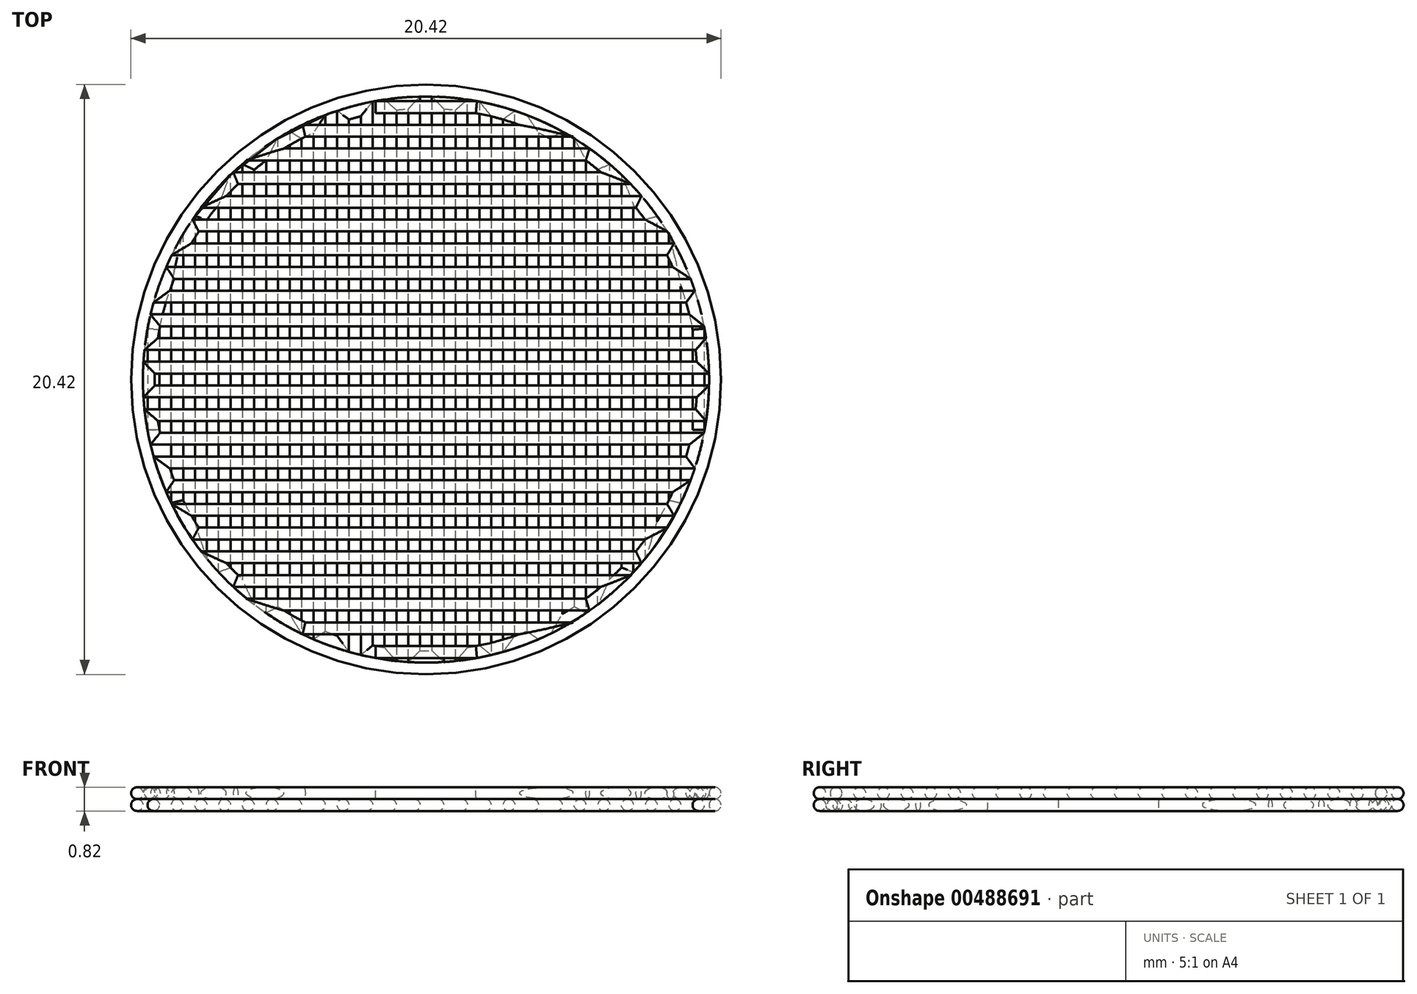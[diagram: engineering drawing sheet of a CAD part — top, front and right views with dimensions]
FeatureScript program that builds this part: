
annotation { "Feature Type Name" : "Feature", "Feature Type Description" : "" }
export const myFeature = defineFeature(function(context is Context, id is Id, definition is map)
    precondition{}
    {
        {
            assignVariable(context, id + "F0", {"name" : "d", "anyValue" : 0.4 * mm});
        }
        {
            var Q0;
            Q0=qCreatedBy(makeId("Top.planeOp"),FACE);
            cPlane(context, id + "F1", {"entities" : qUnion([Q0]), "cplaneType" : CPlaneType.OFFSET, "offset" : getVariable(context, 'd') / 2, "width" : 150 * mm, "height" : 150 * mm});
        }
        {
            var Q0;
            Q0=qCreatedBy(id+"F1.planeOp",FACE);
            var sketch = newSketch(context, id + "F2", { "sketchPlane" : qUnion([Q0])});
            skLineSegment(sketch, "E0.bottom", {"start": v(10, 10) * mm, "end": v(-10, 10) * mm});
            skLineSegment(sketch, "E0.top", {"start": v(10, -10) * mm, "end": v(-10, -10) * mm});
            skLineSegment(sketch, "E0.left", {"start": v(10, 10) * mm, "end": v(10, -10) * mm});
            skLineSegment(sketch, "E0.right", {"start": v(-10, 10) * mm, "end": v(-10, -10) * mm});
            skPoint(sketch, "E0.middle", {"position": v(0, 0) * mm});
            skLineSegment(sketch, "E1", {"start": v(10, -10) * mm, "end": v(9.43, -10) * mm});
            skLineSegment(sketch, "E2", {"start": v(9.43, -10) * mm, "end": v(8.6, -10) * mm});
            skLineSegment(sketch, "E3", {"start": v(8.6, -10) * mm, "end": v(7.8, -10) * mm});
            skLineSegment(sketch, "E4", {"start": v(7.8, -10) * mm, "end": v(6.97, -10) * mm});
            skLineSegment(sketch, "E5", {"start": v(6.97, -10) * mm, "end": v(6.15, -10) * mm});
            skLineSegment(sketch, "E6", {"start": v(6.15, -10) * mm, "end": v(5.33, -10) * mm});
            skLineSegment(sketch, "E7", {"start": v(5.33, -10) * mm, "end": v(4.5, -10) * mm});
            skLineSegment(sketch, "E8", {"start": v(4.5, -10) * mm, "end": v(3.69, -10) * mm});
            skLineSegment(sketch, "E9", {"start": v(3.69, -10) * mm, "end": v(2.87, -10) * mm});
            skLineSegment(sketch, "E10", {"start": v(2.87, -10) * mm, "end": v(2.05, -10) * mm});
            skLineSegment(sketch, "E11", {"start": v(2.05, -10) * mm, "end": v(1.23, -10) * mm});
            skLineSegment(sketch, "E12", {"start": v(-1.23, -10) * mm, "end": v(-2.05, -10) * mm});
            skLineSegment(sketch, "E13", {"start": v(-2.05, -10) * mm, "end": v(-2.87, -10) * mm});
            skLineSegment(sketch, "E14", {"start": v(-2.87, -10) * mm, "end": v(-3.69, -10) * mm});
            skLineSegment(sketch, "E15", {"start": v(-3.69, -10) * mm, "end": v(-4.5, -10) * mm});
            skLineSegment(sketch, "E16", {"start": v(-4.5, -10) * mm, "end": v(-5.33, -10) * mm});
            skLineSegment(sketch, "E17", {"start": v(-5.33, -10) * mm, "end": v(-6.15, -10) * mm});
            skLineSegment(sketch, "E18", {"start": v(-6.15, -10) * mm, "end": v(-6.97, -10) * mm});
            skLineSegment(sketch, "E19", {"start": v(-6.97, -10) * mm, "end": v(-7.8, -10) * mm});
            skLineSegment(sketch, "E20", {"start": v(-7.8, -10) * mm, "end": v(-8.6, -10) * mm});
            skLineSegment(sketch, "E21", {"start": v(-8.6, -10) * mm, "end": v(-9.43, -10) * mm});
            skLineSegment(sketch, "E22", {"start": v(-9.43, -10) * mm, "end": v(-10, -10) * mm});
            skLineSegment(sketch, "E23", {"start": v(9.43, -10) * mm, "end": v(9.43, -1.74) * mm});
            skLineSegment(sketch, "E24", {"start": v(9.43, -1.74) * mm, "end": v(9.43, 1.74) * mm});
            skLineSegment(sketch, "E25", {"start": v(9.43, 1.74) * mm, "end": v(9.43, 10) * mm});
            skLineSegment(sketch, "E26", {"start": v(9.43, 10) * mm, "end": v(10, 10) * mm});
            skLineSegment(sketch, "E27", {"start": v(8.6, -10) * mm, "end": v(8.6, -4.22) * mm});
            skLineSegment(sketch, "E28", {"start": v(8.6, -4.22) * mm, "end": v(8.6, 4.22) * mm});
            skLineSegment(sketch, "E29", {"start": v(8.6, 4.22) * mm, "end": v(8.6, 10) * mm});
            skLineSegment(sketch, "E30", {"start": v(8.6, 10) * mm, "end": v(9.43, 10) * mm});
            skLineSegment(sketch, "E31", {"start": v(7.8, -10) * mm, "end": v(7.8, -5.6) * mm});
            skLineSegment(sketch, "E32", {"start": v(7.8, -5.6) * mm, "end": v(7.8, 5.6) * mm});
            skLineSegment(sketch, "E33", {"start": v(7.8, 5.6) * mm, "end": v(7.8, 10) * mm});
            skLineSegment(sketch, "E34", {"start": v(7.79, 10) * mm, "end": v(8.6, 10) * mm});
            skLineSegment(sketch, "E35", {"start": v(6.97, -10) * mm, "end": v(6.97, -6.59) * mm});
            skLineSegment(sketch, "E36", {"start": v(6.97, -6.59) * mm, "end": v(6.97, 6.59) * mm});
            skLineSegment(sketch, "E37", {"start": v(6.97, 6.59) * mm, "end": v(6.97, 10) * mm});
            skLineSegment(sketch, "E38", {"start": v(6.97, 10) * mm, "end": v(7.79, 10) * mm});
            skLineSegment(sketch, "E39", {"start": v(6.15, -10) * mm, "end": v(6.15, -7.36) * mm});
            skLineSegment(sketch, "E40", {"start": v(6.15, -7.36) * mm, "end": v(6.15, 7.36) * mm});
            skLineSegment(sketch, "E41", {"start": v(6.15, 7.36) * mm, "end": v(6.15, 10) * mm});
            skLineSegment(sketch, "E42", {"start": v(6.15, 10) * mm, "end": v(6.97, 10) * mm});
            skLineSegment(sketch, "E43", {"start": v(5.33, -10) * mm, "end": v(5.33, -7.97) * mm});
            skLineSegment(sketch, "E44", {"start": v(5.33, -7.97) * mm, "end": v(5.33, 7.97) * mm});
            skLineSegment(sketch, "E45", {"start": v(5.33, 7.97) * mm, "end": v(5.33, 10) * mm});
            skLineSegment(sketch, "E46", {"start": v(5.33, 10) * mm, "end": v(6.15, 10) * mm});
            skLineSegment(sketch, "E47", {"start": v(4.5, -10) * mm, "end": v(4.5, -8.46) * mm});
            skLineSegment(sketch, "E48", {"start": v(4.5, -8.46) * mm, "end": v(4.5, 8.46) * mm});
            skLineSegment(sketch, "E49", {"start": v(4.5, 8.46) * mm, "end": v(4.5, 10) * mm});
            skLineSegment(sketch, "E50", {"start": v(4.5, 10) * mm, "end": v(5.33, 10) * mm});
            skLineSegment(sketch, "E51", {"start": v(3.69, -10) * mm, "end": v(3.69, -8.85) * mm});
            skLineSegment(sketch, "E52", {"start": v(3.69, -8.85) * mm, "end": v(3.69, 8.85) * mm});
            skLineSegment(sketch, "E53", {"start": v(3.69, 8.85) * mm, "end": v(3.69, 10) * mm});
            skLineSegment(sketch, "E54", {"start": v(3.69, 10) * mm, "end": v(4.5, 10) * mm});
            skLineSegment(sketch, "E55", {"start": v(2.87, -10) * mm, "end": v(2.87, -9.15) * mm});
            skLineSegment(sketch, "E56", {"start": v(2.87, -9.15) * mm, "end": v(2.87, 9.15) * mm});
            skLineSegment(sketch, "E57", {"start": v(2.87, 9.15) * mm, "end": v(2.87, 10) * mm});
            skLineSegment(sketch, "E58", {"start": v(2.87, 10) * mm, "end": v(3.69, 10) * mm});
            skLineSegment(sketch, "E59", {"start": v(2.05, -10) * mm, "end": v(2.05, -9.37) * mm});
            skLineSegment(sketch, "E60", {"start": v(2.05, -9.37) * mm, "end": v(2.05, 9.37) * mm});
            skLineSegment(sketch, "E61", {"start": v(2.05, 9.37) * mm, "end": v(2.05, 10) * mm});
            skLineSegment(sketch, "E62", {"start": v(2.05, 10) * mm, "end": v(2.87, 10) * mm});
            skLineSegment(sketch, "E63", {"start": v(1.23, -10) * mm, "end": v(1.23, -9.51) * mm});
            skLineSegment(sketch, "E64", {"start": v(1.23, -9.51) * mm, "end": v(1.23, 9.51) * mm});
            skLineSegment(sketch, "E65", {"start": v(1.23, 9.51) * mm, "end": v(1.23, 10) * mm});
            skLineSegment(sketch, "E66", {"start": v(1.23, 10) * mm, "end": v(2.05, 10) * mm});
            skLineSegment(sketch, "E67", {"start": v(-1.23, -10) * mm, "end": v(-1.23, -9.51) * mm});
            skLineSegment(sketch, "E68", {"start": v(-1.23, -9.51) * mm, "end": v(-1.23, 9.51) * mm});
            skLineSegment(sketch, "E69", {"start": v(-1.23, 9.51) * mm, "end": v(-1.23, 10) * mm});
            skLineSegment(sketch, "E70", {"start": v(-2.05, -10) * mm, "end": v(-2.05, -9.37) * mm});
            skLineSegment(sketch, "E71", {"start": v(-2.05, -9.37) * mm, "end": v(-2.05, 9.37) * mm});
            skLineSegment(sketch, "E72", {"start": v(-2.05, 9.37) * mm, "end": v(-2.05, 10) * mm});
            skLineSegment(sketch, "E73", {"start": v(-2.05, 10) * mm, "end": v(-1.23, 10) * mm});
            skLineSegment(sketch, "E74", {"start": v(-2.87, -10) * mm, "end": v(-2.87, -9.15) * mm});
            skLineSegment(sketch, "E75", {"start": v(-2.87, -9.15) * mm, "end": v(-2.87, 9.15) * mm});
            skLineSegment(sketch, "E76", {"start": v(-2.87, 9.15) * mm, "end": v(-2.87, 10) * mm});
            skLineSegment(sketch, "E77", {"start": v(-2.87, 10) * mm, "end": v(-2.05, 10) * mm});
            skLineSegment(sketch, "E78", {"start": v(-3.69, -10) * mm, "end": v(-3.69, -8.85) * mm});
            skLineSegment(sketch, "E79", {"start": v(-3.69, -8.85) * mm, "end": v(-3.69, 8.85) * mm});
            skLineSegment(sketch, "E80", {"start": v(-3.69, 8.85) * mm, "end": v(-3.69, 10) * mm});
            skLineSegment(sketch, "E81", {"start": v(-3.69, 10) * mm, "end": v(-2.87, 10) * mm});
            skLineSegment(sketch, "E82", {"start": v(-4.5, -10) * mm, "end": v(-4.5, -8.46) * mm});
            skLineSegment(sketch, "E83", {"start": v(-4.5, -8.46) * mm, "end": v(-4.5, 8.46) * mm});
            skLineSegment(sketch, "E84", {"start": v(-4.5, 8.46) * mm, "end": v(-4.5, 10) * mm});
            skLineSegment(sketch, "E85", {"start": v(-4.5, 10) * mm, "end": v(-3.69, 10) * mm});
            skLineSegment(sketch, "E86", {"start": v(-5.33, -10) * mm, "end": v(-5.33, -7.97) * mm});
            skLineSegment(sketch, "E87", {"start": v(-5.33, -7.97) * mm, "end": v(-5.33, 7.97) * mm});
            skLineSegment(sketch, "E88", {"start": v(-5.33, 7.97) * mm, "end": v(-5.33, 10) * mm});
            skLineSegment(sketch, "E89", {"start": v(-5.33, 10) * mm, "end": v(-4.5, 10) * mm});
            skLineSegment(sketch, "E90", {"start": v(-6.15, -10) * mm, "end": v(-6.15, -7.36) * mm});
            skLineSegment(sketch, "E91", {"start": v(-6.15, -7.36) * mm, "end": v(-6.15, 7.36) * mm});
            skLineSegment(sketch, "E92", {"start": v(-6.15, 7.36) * mm, "end": v(-6.15, 10) * mm});
            skLineSegment(sketch, "E93", {"start": v(-6.15, 10) * mm, "end": v(-5.33, 10) * mm});
            skLineSegment(sketch, "E94", {"start": v(-6.97, -10) * mm, "end": v(-6.97, -6.59) * mm});
            skLineSegment(sketch, "E95", {"start": v(-6.97, -6.59) * mm, "end": v(-6.97, 6.59) * mm});
            skLineSegment(sketch, "E96", {"start": v(-6.97, 6.59) * mm, "end": v(-6.97, 10) * mm});
            skLineSegment(sketch, "E97", {"start": v(-6.97, 10) * mm, "end": v(-6.15, 10) * mm});
            skLineSegment(sketch, "E98", {"start": v(-7.8, -10) * mm, "end": v(-7.8, -5.6) * mm});
            skLineSegment(sketch, "E99", {"start": v(-7.8, -5.6) * mm, "end": v(-7.8, 5.6) * mm});
            skLineSegment(sketch, "E100", {"start": v(-7.8, 5.6) * mm, "end": v(-7.8, 10) * mm});
            skLineSegment(sketch, "E101", {"start": v(-7.8, 10) * mm, "end": v(-6.97, 10) * mm});
            skLineSegment(sketch, "E102", {"start": v(-8.6, -10) * mm, "end": v(-8.6, -4.22) * mm});
            skLineSegment(sketch, "E103", {"start": v(-8.6, -4.22) * mm, "end": v(-8.6, 4.22) * mm});
            skLineSegment(sketch, "E104", {"start": v(-8.6, 4.22) * mm, "end": v(-8.6, 10) * mm});
            skLineSegment(sketch, "E105", {"start": v(-8.6, 10) * mm, "end": v(-7.8, 10) * mm});
            skLineSegment(sketch, "E106", {"start": v(-9.43, -10) * mm, "end": v(-9.43, -1.74) * mm});
            skLineSegment(sketch, "E107", {"start": v(-9.43, -1.74) * mm, "end": v(-9.43, 1.74) * mm});
            skLineSegment(sketch, "E108", {"start": v(-9.43, 1.74) * mm, "end": v(-9.43, 10) * mm});
            skLineSegment(sketch, "E109", {"start": v(-9.43, 10) * mm, "end": v(-8.6, 10) * mm});
            skLineSegment(sketch, "E110", {"start": v(-10, 10) * mm, "end": v(-9.43, 10) * mm});
            skArc(sketch, "E111", {"start": v(9.43, 1.74) * mm, "mid": v(9.1, 3.01) * mm, "end": v(8.61, 4.22) * mm});
            skArc(sketch, "E112", {"start": v(7.8, 5.6) * mm, "mid": v(7.4, 6.1) * mm, "end": v(6.97, 6.59) * mm});
            skArc(sketch, "E113", {"start": v(6.15, 7.36) * mm, "mid": v(5.75, 7.68) * mm, "end": v(5.33, 7.97) * mm});
            skArc(sketch, "E114", {"start": v(4.51, 8.46) * mm, "mid": v(4.1, 8.67) * mm, "end": v(3.7, 8.85) * mm});
            skArc(sketch, "E115", {"start": v(2.87, 9.15) * mm, "mid": v(2.46, 9.27) * mm, "end": v(2.05, 9.37) * mm});
            skArc(sketch, "E116", {"start": v(1.23, -9.51) * mm, "mid": v(1.64, -9.45) * mm, "end": v(2.05, -9.37) * mm});
            skArc(sketch, "E117", {"start": v(2.87, -9.15) * mm, "mid": v(3.28, -9.01) * mm, "end": v(3.69, -8.85) * mm});
            skArc(sketch, "E118", {"start": v(4.51, -8.46) * mm, "mid": v(4.93, -8.23) * mm, "end": v(5.33, -7.97) * mm});
            skArc(sketch, "E119", {"start": v(6.15, -7.36) * mm, "mid": v(6.57, -6.98) * mm, "end": v(6.97, -6.59) * mm});
            skArc(sketch, "E120", {"start": v(7.8, -5.6) * mm, "mid": v(8.23, -4.93) * mm, "end": v(8.6, -4.22) * mm});
            skLineSegment(sketch, "E121", {"start": v(1.23, -10) * mm, "end": v(0.4, -10) * mm});
            skLineSegment(sketch, "E122", {"start": v(0.4, -10) * mm, "end": v(-0.4, -10) * mm});
            skLineSegment(sketch, "E123", {"start": v(-0.4, -10) * mm, "end": v(-1.23, -10) * mm});
            skLineSegment(sketch, "E124", {"start": v(0.4, -10) * mm, "end": v(0.4, -9.58) * mm});
            skLineSegment(sketch, "E125", {"start": v(0.4, -9.58) * mm, "end": v(0.4, 9.58) * mm});
            skLineSegment(sketch, "E126", {"start": v(0.4, 9.58) * mm, "end": v(0.4, 10) * mm});
            skLineSegment(sketch, "E127", {"start": v(0.4, 10) * mm, "end": v(1.23, 10) * mm});
            skLineSegment(sketch, "E128", {"start": v(0.4, 10) * mm, "end": v(-0.4, 10) * mm});
            skLineSegment(sketch, "E129", {"start": v(-0.4, 10) * mm, "end": v(-1.23, 10) * mm});
            skLineSegment(sketch, "E130", {"start": v(-0.4, 10) * mm, "end": v(-0.4, 9.58) * mm});
            skLineSegment(sketch, "E131", {"start": v(-0.4, 9.58) * mm, "end": v(-0.4, -9.58) * mm});
            skLineSegment(sketch, "E132", {"start": v(-0.41, -9.58) * mm, "end": v(-0.4, -10) * mm});
            skCircle(sketch, "E133", {"center": v(0, 0) * mm, "radius": 10 * mm});
            skArc(sketch, "E134", {"start": v(1.23, 9.51) * mm, "mid": v(0.82, 9.55) * mm, "end": v(0.41, 9.58) * mm});
            skArc(sketch, "E135", {"start": v(-0.4, 9.58) * mm, "mid": v(-0.82, 9.55) * mm, "end": v(-1.23, 9.51) * mm});
            skArc(sketch, "E136", {"start": v(-2.05, 9.37) * mm, "mid": v(-2.46, 9.27) * mm, "end": v(-2.87, 9.15) * mm});
            skArc(sketch, "E137", {"start": v(-3.69, 8.85) * mm, "mid": v(-4.1, 8.67) * mm, "end": v(-4.51, 8.46) * mm});
            skArc(sketch, "E138", {"start": v(-5.33, 7.97) * mm, "mid": v(-5.75, 7.68) * mm, "end": v(-6.15, 7.36) * mm});
            skArc(sketch, "E139", {"start": v(-6.97, 6.59) * mm, "mid": v(-7.4, 6.1) * mm, "end": v(-7.79, 5.6) * mm});
            skArc(sketch, "E140", {"start": v(-8.6, 4.22) * mm, "mid": v(-9.1, 3.01) * mm, "end": v(-9.43, 1.74) * mm});
            skArc(sketch, "E141", {"start": v(0.41, -9.58) * mm, "mid": v(0, -9.6) * mm, "end": v(-0.4, -9.58) * mm});
            skArc(sketch, "E142", {"start": v(-1.23, -9.51) * mm, "mid": v(-1.64, -9.45) * mm, "end": v(-2.05, -9.37) * mm});
            skArc(sketch, "E143", {"start": v(-2.87, -9.15) * mm, "mid": v(-3.28, -9.01) * mm, "end": v(-3.69, -8.85) * mm});
            skArc(sketch, "E144", {"start": v(-4.51, -8.46) * mm, "mid": v(-4.93, -8.23) * mm, "end": v(-5.33, -7.97) * mm});
            skArc(sketch, "E145", {"start": v(-6.15, -7.36) * mm, "mid": v(-6.57, -6.98) * mm, "end": v(-6.97, -6.59) * mm});
            skArc(sketch, "E146", {"start": v(-7.8, -5.6) * mm, "mid": v(-8.23, -4.93) * mm, "end": v(-8.61, -4.22) * mm});
            skSolve(sketch);
        }
        {
            var Q0;
            Q0=qCreatedBy(makeId("Front.planeOp"),FACE);
            var sketch = newSketch(context, id + "F3", { "sketchPlane" : qUnion([Q0])});
            skCircle(sketch, "E147", {"center": v(-10, 0.2) * mm, "radius": 0.2 * mm});
            skSolve(sketch);
        }
        {
            var Q0;
            Q0=makeQuery(id+"F3.imprint","IMPRINT",FACE,{"disambiguationData":[TD([[makeQuery(id+"F3.imprint","IMPRINT",EDGE,{"derivedFrom":sQuery(id+"F3.wireOp",EDGE,"E147")}),1.0]])]});
            var Q1;
            Q1=sQuery(id+"F3.wireOp",EDGE,"E147");
            var Q2;
            Q2=sQuery(id+"F2.wireOp",EDGE,"E133");
            sweep(context, id + "F4", {"profiles" : qUnion([Q0]), "surfaceProfiles" : qUnion([Q1]), "path" : qUnion([Q2])});
        }
        {
            var Q0;
            Q0=sQuery(id+"F2.wireOp",EDGE,"E24");
            var Q1;
            Q1=sQuery(id+"F2.wireOp",VERTEX,"E24.start");
            cPlane(context, id + "F5", {"entities" : qUnion([Q0, Q1]), "cplaneType" : CPlaneType.LINE_POINT, "offset" : 25 * mm, "width" : 150 * mm, "height" : 150 * mm});
        }
        {
            var Q0;
            Q0=qCreatedBy(id+"F5.planeOp",FACE);
            var sketch = newSketch(context, id + "F6", { "sketchPlane" : qUnion([Q0])});
            skCircle(sketch, "E148", {"center": v(-9.43, 0.2) * mm, "radius": 0.2 * mm});
            skSolve(sketch);
        }
        {
            var Q0;
            Q0=qSketchRegion(id+"F6",true);
            var Q1;
            Q1=sQuery(id+"F2.wireOp",EDGE,"E24");
            var Q2;
            Q2=sQuery(id+"F2.wireOp",EDGE,"E111");
            var Q3;
            Q3=sQuery(id+"F2.wireOp",EDGE,"E112");
            var Q4;
            Q4=sQuery(id+"F2.wireOp",EDGE,"E113");
            var Q5;
            Q5=sQuery(id+"F2.wireOp",EDGE,"E114");
            var Q6;
            Q6=sQuery(id+"F2.wireOp",EDGE,"E115");
            var Q7;
            Q7=sQuery(id+"F2.wireOp",EDGE,"E134");
            var Q8;
            Q8=sQuery(id+"F2.wireOp",EDGE,"E135");
            var Q9;
            Q9=sQuery(id+"F2.wireOp",EDGE,"E136");
            var Q10;
            Q10=sQuery(id+"F2.wireOp",EDGE,"E137");
            var Q11;
            Q11=sQuery(id+"F2.wireOp",EDGE,"E138");
            var Q12;
            Q12=sQuery(id+"F2.wireOp",EDGE,"E139");
            var Q13;
            Q13=sQuery(id+"F2.wireOp",EDGE,"E140");
            var Q14;
            Q14=sQuery(id+"F2.wireOp",EDGE,"E107");
            var Q15;
            Q15=sQuery(id+"F2.wireOp",EDGE,"E146");
            var Q16;
            Q16=sQuery(id+"F2.wireOp",EDGE,"E145");
            var Q17;
            Q17=sQuery(id+"F2.wireOp",EDGE,"E144");
            var Q18;
            Q18=sQuery(id+"F2.wireOp",EDGE,"E143");
            var Q19;
            Q19=sQuery(id+"F2.wireOp",EDGE,"E142");
            var Q20;
            Q20=sQuery(id+"F2.wireOp",EDGE,"E141");
            var Q21;
            Q21=sQuery(id+"F2.wireOp",EDGE,"E116");
            var Q22;
            Q22=sQuery(id+"F2.wireOp",EDGE,"E117");
            var Q23;
            Q23=sQuery(id+"F2.wireOp",EDGE,"E118");
            var Q24;
            Q24=sQuery(id+"F2.wireOp",EDGE,"E119");
            var Q25;
            Q25=sQuery(id+"F2.wireOp",EDGE,"E120");
            var Q26;
            Q26=sQuery(id+"F2.wireOp",EDGE,"E28");
            var Q27;
            Q27=sQuery(id+"F2.wireOp",EDGE,"E32");
            var Q28;
            Q28=sQuery(id+"F2.wireOp",EDGE,"E36");
            var Q29;
            Q29=sQuery(id+"F2.wireOp",EDGE,"E40");
            var Q30;
            Q30=sQuery(id+"F2.wireOp",EDGE,"E44");
            var Q31;
            Q31=sQuery(id+"F2.wireOp",EDGE,"E48");
            var Q32;
            Q32=sQuery(id+"F2.wireOp",EDGE,"E52");
            var Q33;
            Q33=sQuery(id+"F2.wireOp",EDGE,"E56");
            var Q34;
            Q34=sQuery(id+"F2.wireOp",EDGE,"E60");
            var Q35;
            Q35=sQuery(id+"F2.wireOp",EDGE,"E64");
            var Q36;
            Q36=sQuery(id+"F2.wireOp",EDGE,"E125");
            var Q37;
            Q37=sQuery(id+"F2.wireOp",EDGE,"E131");
            var Q38;
            Q38=sQuery(id+"F2.wireOp",EDGE,"E68");
            var Q39;
            Q39=sQuery(id+"F2.wireOp",EDGE,"E71");
            var Q40;
            Q40=sQuery(id+"F2.wireOp",EDGE,"E75");
            var Q41;
            Q41=sQuery(id+"F2.wireOp",EDGE,"E79");
            var Q42;
            Q42=sQuery(id+"F2.wireOp",EDGE,"E83");
            var Q43;
            Q43=sQuery(id+"F2.wireOp",EDGE,"E87");
            var Q44;
            Q44=sQuery(id+"F2.wireOp",EDGE,"E91");
            var Q45;
            Q45=sQuery(id+"F2.wireOp",EDGE,"E95");
            var Q46;
            Q46=sQuery(id+"F2.wireOp",EDGE,"E99");
            var Q47;
            Q47=sQuery(id+"F2.wireOp",EDGE,"E103");
            sweep(context, id + "F7", {"profiles" : qUnion([Q0]), "path" : qUnion([Q1, Q2, Q3, Q4, Q5, Q6, Q7, Q8, Q9, Q10, Q11, Q12, Q13, Q14, Q15, Q16, Q17, Q18, Q19, Q20, Q21, Q22, Q23, Q24, Q25, Q26, Q27, Q28, Q29, Q30, Q31, Q32, Q33, Q34, Q35, Q36, Q37, Q38, Q39, Q40, Q41, Q42, Q43, Q44, Q45, Q46, Q47])});
        }
        {
            var Q0;
            Q0=qCreatedBy(id+"F1.planeOp",FACE);
            cPlane(context, id + "F8", {"entities" : qUnion([Q0]), "cplaneType" : CPlaneType.OFFSET, "offset" : getVariable(context, 'd'), "width" : 150 * mm, "height" : 150 * mm});
        }
        {
            var Q0;
            Q0=qCreatedBy(id+"F8.planeOp",FACE);
            var sketch = newSketch(context, id + "F9", { "sketchPlane" : qUnion([Q0])});
            skLineSegment(sketch, "E149.bottom", {"start": v(10, -10) * mm, "end": v(10, 10) * mm});
            skLineSegment(sketch, "E149.top", {"start": v(-10, -10) * mm, "end": v(-10, 10) * mm});
            skLineSegment(sketch, "E149.left", {"start": v(10, -10) * mm, "end": v(-10, -10) * mm});
            skLineSegment(sketch, "E149.right", {"start": v(10, 10) * mm, "end": v(-10, 10) * mm});
            skPoint(sketch, "E149.middle", {"position": v(0, 0) * mm});
            skLineSegment(sketch, "E150", {"start": v(-10, -10) * mm, "end": v(-10, -9.43) * mm});
            skLineSegment(sketch, "E151", {"start": v(-10, -9.43) * mm, "end": v(-10, -8.6) * mm});
            skLineSegment(sketch, "E152", {"start": v(-10, -8.6) * mm, "end": v(-10, -7.8) * mm});
            skLineSegment(sketch, "E153", {"start": v(-10, -7.8) * mm, "end": v(-10, -6.97) * mm});
            skLineSegment(sketch, "E154", {"start": v(-10, -6.97) * mm, "end": v(-10, -6.15) * mm});
            skLineSegment(sketch, "E155", {"start": v(-10, -6.15) * mm, "end": v(-10, -5.33) * mm});
            skLineSegment(sketch, "E156", {"start": v(-10, -5.33) * mm, "end": v(-10, -4.51) * mm});
            skLineSegment(sketch, "E157", {"start": v(-10, -4.51) * mm, "end": v(-10, -3.7) * mm});
            skLineSegment(sketch, "E158", {"start": v(-10, -3.7) * mm, "end": v(-10, -2.87) * mm});
            skLineSegment(sketch, "E159", {"start": v(-10, -2.87) * mm, "end": v(-10, -2.05) * mm});
            skLineSegment(sketch, "E160", {"start": v(-10, -2.05) * mm, "end": v(-10, -1.23) * mm});
            skLineSegment(sketch, "E161", {"start": v(-10, 1.23) * mm, "end": v(-10, 2.05) * mm});
            skLineSegment(sketch, "E162", {"start": v(-10, 2.05) * mm, "end": v(-10, 2.87) * mm});
            skLineSegment(sketch, "E163", {"start": v(-10, 2.87) * mm, "end": v(-10, 3.7) * mm});
            skLineSegment(sketch, "E164", {"start": v(-10, 3.7) * mm, "end": v(-10, 4.51) * mm});
            skLineSegment(sketch, "E165", {"start": v(-10, 4.51) * mm, "end": v(-10, 5.33) * mm});
            skLineSegment(sketch, "E166", {"start": v(-10, 5.33) * mm, "end": v(-10, 6.15) * mm});
            skLineSegment(sketch, "E167", {"start": v(-10, 6.15) * mm, "end": v(-10, 6.97) * mm});
            skLineSegment(sketch, "E168", {"start": v(-10, 6.97) * mm, "end": v(-10, 7.8) * mm});
            skLineSegment(sketch, "E169", {"start": v(-10, 7.8) * mm, "end": v(-10, 8.61) * mm});
            skLineSegment(sketch, "E170", {"start": v(-10, 8.61) * mm, "end": v(-10, 9.43) * mm});
            skLineSegment(sketch, "E171", {"start": v(-10, 9.43) * mm, "end": v(-10, 10) * mm});
            skLineSegment(sketch, "E172", {"start": v(-10, -9.43) * mm, "end": v(-1.74, -9.43) * mm});
            skLineSegment(sketch, "E173", {"start": v(-1.74, -9.43) * mm, "end": v(1.74, -9.43) * mm});
            skLineSegment(sketch, "E174", {"start": v(1.74, -9.43) * mm, "end": v(10, -9.43) * mm});
            skLineSegment(sketch, "E175", {"start": v(10, -9.43) * mm, "end": v(10, -10) * mm});
            skLineSegment(sketch, "E176", {"start": v(-10, -8.6) * mm, "end": v(-4.22, -8.6) * mm});
            skLineSegment(sketch, "E177", {"start": v(-4.22, -8.6) * mm, "end": v(4.22, -8.6) * mm});
            skLineSegment(sketch, "E178", {"start": v(4.22, -8.6) * mm, "end": v(10, -8.6) * mm});
            skLineSegment(sketch, "E179", {"start": v(10, -8.6) * mm, "end": v(10, -9.43) * mm});
            skLineSegment(sketch, "E180", {"start": v(-10, -7.8) * mm, "end": v(-5.6, -7.8) * mm});
            skLineSegment(sketch, "E181", {"start": v(-5.6, -7.8) * mm, "end": v(5.6, -7.8) * mm});
            skLineSegment(sketch, "E182", {"start": v(5.6, -7.8) * mm, "end": v(10, -7.8) * mm});
            skLineSegment(sketch, "E183", {"start": v(10, -7.8) * mm, "end": v(10, -8.6) * mm});
            skLineSegment(sketch, "E184", {"start": v(-10, -6.97) * mm, "end": v(-6.59, -6.97) * mm});
            skLineSegment(sketch, "E185", {"start": v(-6.59, -6.97) * mm, "end": v(6.59, -6.97) * mm});
            skLineSegment(sketch, "E186", {"start": v(6.59, -6.97) * mm, "end": v(10, -6.97) * mm});
            skLineSegment(sketch, "E187", {"start": v(10, -6.97) * mm, "end": v(10, -7.8) * mm});
            skLineSegment(sketch, "E188", {"start": v(-10, -6.15) * mm, "end": v(-7.36, -6.15) * mm});
            skLineSegment(sketch, "E189", {"start": v(-7.36, -6.15) * mm, "end": v(7.36, -6.15) * mm});
            skLineSegment(sketch, "E190", {"start": v(7.36, -6.15) * mm, "end": v(10, -6.15) * mm});
            skLineSegment(sketch, "E191", {"start": v(10, -6.15) * mm, "end": v(10, -6.97) * mm});
            skLineSegment(sketch, "E192", {"start": v(-10, -5.33) * mm, "end": v(-7.97, -5.33) * mm});
            skLineSegment(sketch, "E193", {"start": v(-7.97, -5.33) * mm, "end": v(7.97, -5.33) * mm});
            skLineSegment(sketch, "E194", {"start": v(7.97, -5.33) * mm, "end": v(10, -5.33) * mm});
            skLineSegment(sketch, "E195", {"start": v(10, -5.33) * mm, "end": v(10, -6.15) * mm});
            skLineSegment(sketch, "E196", {"start": v(-10, -4.51) * mm, "end": v(-8.46, -4.51) * mm});
            skLineSegment(sketch, "E197", {"start": v(-8.46, -4.51) * mm, "end": v(8.46, -4.51) * mm});
            skLineSegment(sketch, "E198", {"start": v(8.46, -4.51) * mm, "end": v(10, -4.51) * mm});
            skLineSegment(sketch, "E199", {"start": v(10, -4.51) * mm, "end": v(10, -5.33) * mm});
            skLineSegment(sketch, "E200", {"start": v(-10, -3.7) * mm, "end": v(-8.85, -3.7) * mm});
            skLineSegment(sketch, "E201", {"start": v(-8.85, -3.7) * mm, "end": v(8.85, -3.7) * mm});
            skLineSegment(sketch, "E202", {"start": v(8.85, -3.7) * mm, "end": v(10, -3.7) * mm});
            skLineSegment(sketch, "E203", {"start": v(10, -3.7) * mm, "end": v(10, -4.51) * mm});
            skLineSegment(sketch, "E204", {"start": v(-10, -2.87) * mm, "end": v(-9.15, -2.87) * mm});
            skLineSegment(sketch, "E205", {"start": v(-9.15, -2.87) * mm, "end": v(9.15, -2.87) * mm});
            skLineSegment(sketch, "E206", {"start": v(9.15, -2.87) * mm, "end": v(10, -2.87) * mm});
            skLineSegment(sketch, "E207", {"start": v(10, -2.87) * mm, "end": v(10, -3.7) * mm});
            skLineSegment(sketch, "E208", {"start": v(-10, -2.05) * mm, "end": v(-9.37, -2.05) * mm});
            skLineSegment(sketch, "E209", {"start": v(-9.37, -2.05) * mm, "end": v(9.37, -2.05) * mm});
            skLineSegment(sketch, "E210", {"start": v(9.37, -2.05) * mm, "end": v(10, -2.05) * mm});
            skLineSegment(sketch, "E211", {"start": v(10, -2.05) * mm, "end": v(10, -2.87) * mm});
            skLineSegment(sketch, "E212", {"start": v(-10, -1.23) * mm, "end": v(-9.51, -1.23) * mm});
            skLineSegment(sketch, "E213", {"start": v(-9.51, -1.23) * mm, "end": v(9.51, -1.23) * mm});
            skLineSegment(sketch, "E214", {"start": v(9.51, -1.23) * mm, "end": v(10, -1.23) * mm});
            skLineSegment(sketch, "E215", {"start": v(10, -1.23) * mm, "end": v(10, -2.05) * mm});
            skLineSegment(sketch, "E216", {"start": v(-10, 1.23) * mm, "end": v(-9.51, 1.23) * mm});
            skLineSegment(sketch, "E217", {"start": v(-9.51, 1.23) * mm, "end": v(9.51, 1.23) * mm});
            skLineSegment(sketch, "E218", {"start": v(9.51, 1.23) * mm, "end": v(10, 1.23) * mm});
            skLineSegment(sketch, "E219", {"start": v(-10, 2.05) * mm, "end": v(-9.37, 2.05) * mm});
            skLineSegment(sketch, "E220", {"start": v(-9.37, 2.05) * mm, "end": v(9.37, 2.05) * mm});
            skLineSegment(sketch, "E221", {"start": v(9.37, 2.05) * mm, "end": v(10, 2.05) * mm});
            skLineSegment(sketch, "E222", {"start": v(10, 2.05) * mm, "end": v(10, 1.23) * mm});
            skLineSegment(sketch, "E223", {"start": v(-10, 2.87) * mm, "end": v(-9.15, 2.87) * mm});
            skLineSegment(sketch, "E224", {"start": v(-9.15, 2.87) * mm, "end": v(9.15, 2.87) * mm});
            skLineSegment(sketch, "E225", {"start": v(9.15, 2.87) * mm, "end": v(10, 2.87) * mm});
            skLineSegment(sketch, "E226", {"start": v(10, 2.87) * mm, "end": v(10, 2.05) * mm});
            skLineSegment(sketch, "E227", {"start": v(-10, 3.7) * mm, "end": v(-8.85, 3.7) * mm});
            skLineSegment(sketch, "E228", {"start": v(-8.85, 3.7) * mm, "end": v(8.85, 3.7) * mm});
            skLineSegment(sketch, "E229", {"start": v(8.85, 3.7) * mm, "end": v(10, 3.7) * mm});
            skLineSegment(sketch, "E230", {"start": v(10, 3.7) * mm, "end": v(10, 2.87) * mm});
            skLineSegment(sketch, "E231", {"start": v(-10, 4.51) * mm, "end": v(-8.46, 4.51) * mm});
            skLineSegment(sketch, "E232", {"start": v(-8.46, 4.51) * mm, "end": v(8.46, 4.51) * mm});
            skLineSegment(sketch, "E233", {"start": v(8.46, 4.51) * mm, "end": v(10, 4.51) * mm});
            skLineSegment(sketch, "E234", {"start": v(10, 4.51) * mm, "end": v(10, 3.7) * mm});
            skLineSegment(sketch, "E235", {"start": v(-10, 5.33) * mm, "end": v(-7.97, 5.33) * mm});
            skLineSegment(sketch, "E236", {"start": v(-7.97, 5.33) * mm, "end": v(7.97, 5.33) * mm});
            skLineSegment(sketch, "E237", {"start": v(7.97, 5.33) * mm, "end": v(10, 5.33) * mm});
            skLineSegment(sketch, "E238", {"start": v(10, 5.33) * mm, "end": v(10, 4.51) * mm});
            skLineSegment(sketch, "E239", {"start": v(-10, 6.15) * mm, "end": v(-7.36, 6.15) * mm});
            skLineSegment(sketch, "E240", {"start": v(-7.36, 6.15) * mm, "end": v(7.36, 6.15) * mm});
            skLineSegment(sketch, "E241", {"start": v(7.36, 6.15) * mm, "end": v(10, 6.15) * mm});
            skLineSegment(sketch, "E242", {"start": v(10, 6.15) * mm, "end": v(10, 5.33) * mm});
            skLineSegment(sketch, "E243", {"start": v(-10, 6.97) * mm, "end": v(-6.59, 6.97) * mm});
            skLineSegment(sketch, "E244", {"start": v(-6.59, 6.97) * mm, "end": v(6.59, 6.97) * mm});
            skLineSegment(sketch, "E245", {"start": v(6.59, 6.97) * mm, "end": v(10, 6.97) * mm});
            skLineSegment(sketch, "E246", {"start": v(10, 6.97) * mm, "end": v(10, 6.15) * mm});
            skLineSegment(sketch, "E247", {"start": v(-10, 7.8) * mm, "end": v(-5.6, 7.8) * mm});
            skLineSegment(sketch, "E248", {"start": v(-5.6, 7.8) * mm, "end": v(5.6, 7.8) * mm});
            skLineSegment(sketch, "E249", {"start": v(5.6, 7.8) * mm, "end": v(10, 7.8) * mm});
            skLineSegment(sketch, "E250", {"start": v(10, 7.8) * mm, "end": v(10, 6.97) * mm});
            skLineSegment(sketch, "E251", {"start": v(-10, 8.61) * mm, "end": v(-4.22, 8.61) * mm});
            skLineSegment(sketch, "E252", {"start": v(-4.22, 8.61) * mm, "end": v(4.22, 8.61) * mm});
            skLineSegment(sketch, "E253", {"start": v(4.22, 8.61) * mm, "end": v(10, 8.61) * mm});
            skLineSegment(sketch, "E254", {"start": v(10, 8.61) * mm, "end": v(10, 7.8) * mm});
            skLineSegment(sketch, "E255", {"start": v(-10, 9.43) * mm, "end": v(-1.74, 9.43) * mm});
            skLineSegment(sketch, "E256", {"start": v(-1.74, 9.43) * mm, "end": v(1.74, 9.43) * mm});
            skLineSegment(sketch, "E257", {"start": v(1.74, 9.43) * mm, "end": v(10, 9.43) * mm});
            skLineSegment(sketch, "E258", {"start": v(10, 9.43) * mm, "end": v(10, 8.61) * mm});
            skLineSegment(sketch, "E259", {"start": v(10, 10) * mm, "end": v(10, 9.43) * mm});
            skArc(sketch, "E260", {"start": v(1.74, -9.43) * mm, "mid": v(3.01, -9.1) * mm, "end": v(4.22, -8.6) * mm});
            skArc(sketch, "E261", {"start": v(5.6, -7.79) * mm, "mid": v(6.1, -7.4) * mm, "end": v(6.59, -6.97) * mm});
            skArc(sketch, "E262", {"start": v(7.36, -6.15) * mm, "mid": v(7.68, -5.75) * mm, "end": v(7.97, -5.33) * mm});
            skArc(sketch, "E263", {"start": v(8.46, -4.5) * mm, "mid": v(8.67, -4.1) * mm, "end": v(8.85, -3.69) * mm});
            skArc(sketch, "E264", {"start": v(9.15, -2.87) * mm, "mid": v(9.27, -2.46) * mm, "end": v(9.37, -2.05) * mm});
            skArc(sketch, "E265", {"start": v(-9.51, -1.23) * mm, "mid": v(-9.45, -1.64) * mm, "end": v(-9.37, -2.05) * mm});
            skArc(sketch, "E266", {"start": v(-9.15, -2.87) * mm, "mid": v(-9.01, -3.28) * mm, "end": v(-8.85, -3.69) * mm});
            skArc(sketch, "E267", {"start": v(-8.46, -4.5) * mm, "mid": v(-8.23, -4.93) * mm, "end": v(-7.97, -5.33) * mm});
            skArc(sketch, "E268", {"start": v(-7.36, -6.15) * mm, "mid": v(-6.98, -6.57) * mm, "end": v(-6.59, -6.97) * mm});
            skArc(sketch, "E269", {"start": v(-5.6, -7.79) * mm, "mid": v(-4.93, -8.23) * mm, "end": v(-4.22, -8.6) * mm});
            skLineSegment(sketch, "E270", {"start": v(-10, -1.23) * mm, "end": v(-10, -0.41) * mm});
            skLineSegment(sketch, "E271", {"start": v(-10, -0.41) * mm, "end": v(-10, 0.4) * mm});
            skLineSegment(sketch, "E272", {"start": v(-10, 0.4) * mm, "end": v(-10, 1.23) * mm});
            skLineSegment(sketch, "E273", {"start": v(-10, -0.41) * mm, "end": v(-9.58, -0.41) * mm});
            skLineSegment(sketch, "E274", {"start": v(-9.58, -0.41) * mm, "end": v(9.58, -0.41) * mm});
            skLineSegment(sketch, "E275", {"start": v(9.58, -0.41) * mm, "end": v(10, -0.41) * mm});
            skLineSegment(sketch, "E276", {"start": v(10, -0.41) * mm, "end": v(10, -1.23) * mm});
            skLineSegment(sketch, "E277", {"start": v(10, -0.41) * mm, "end": v(10, 0.41) * mm});
            skLineSegment(sketch, "E278", {"start": v(10, 0.41) * mm, "end": v(10, 1.23) * mm});
            skLineSegment(sketch, "E279", {"start": v(10, 0.41) * mm, "end": v(9.58, 0.41) * mm});
            skLineSegment(sketch, "E280", {"start": v(9.58, 0.41) * mm, "end": v(-9.58, 0.41) * mm});
            skLineSegment(sketch, "E281", {"start": v(-9.58, 0.41) * mm, "end": v(-10, 0.4) * mm});
            skCircle(sketch, "E282", {"center": v(0, 0) * mm, "radius": 10 * mm});
            skArc(sketch, "E283", {"start": v(9.51, -1.23) * mm, "mid": v(9.55, -0.82) * mm, "end": v(9.58, -0.41) * mm});
            skArc(sketch, "E284", {"start": v(9.58, 0.41) * mm, "mid": v(9.55, 0.82) * mm, "end": v(9.51, 1.23) * mm});
            skArc(sketch, "E285", {"start": v(9.37, 2.05) * mm, "mid": v(9.27, 2.46) * mm, "end": v(9.15, 2.87) * mm});
            skArc(sketch, "E286", {"start": v(8.85, 3.7) * mm, "mid": v(8.67, 4.1) * mm, "end": v(8.46, 4.51) * mm});
            skArc(sketch, "E287", {"start": v(7.97, 5.33) * mm, "mid": v(7.68, 5.75) * mm, "end": v(7.36, 6.15) * mm});
            skArc(sketch, "E288", {"start": v(6.59, 6.97) * mm, "mid": v(6.1, 7.4) * mm, "end": v(5.6, 7.8) * mm});
            skArc(sketch, "E289", {"start": v(4.22, 8.61) * mm, "mid": v(3.01, 9.1) * mm, "end": v(1.74, 9.43) * mm});
            skArc(sketch, "E290", {"start": v(-9.58, -0.41) * mm, "mid": v(-9.6, 0) * mm, "end": v(-9.58, 0.41) * mm});
            skArc(sketch, "E291", {"start": v(-9.51, 1.23) * mm, "mid": v(-9.45, 1.64) * mm, "end": v(-9.37, 2.05) * mm});
            skArc(sketch, "E292", {"start": v(-9.15, 2.87) * mm, "mid": v(-9.01, 3.28) * mm, "end": v(-8.85, 3.7) * mm});
            skArc(sketch, "E293", {"start": v(-8.46, 4.51) * mm, "mid": v(-8.23, 4.93) * mm, "end": v(-7.97, 5.33) * mm});
            skArc(sketch, "E294", {"start": v(-7.36, 6.15) * mm, "mid": v(-6.98, 6.57) * mm, "end": v(-6.59, 6.97) * mm});
            skArc(sketch, "E295", {"start": v(-5.6, 7.8) * mm, "mid": v(-4.93, 8.23) * mm, "end": v(-4.22, 8.61) * mm});
            skSolve(sketch);
        }
        {
            var Q0;
            Q0=qCreatedBy(makeId("Right.planeOp"),FACE);
            var sketch = newSketch(context, id + "F10", { "sketchPlane" : qUnion([Q0])});
            skCircle(sketch, "E296", {"center": v(10, 0.61) * mm, "radius": 0.2 * mm});
            skSolve(sketch);
        }
        {
            var Q0;
            Q0=makeQuery(id+"F10.imprint","IMPRINT",FACE,{"disambiguationData":[TD([[makeQuery(id+"F10.imprint","IMPRINT",EDGE,{"derivedFrom":sQuery(id+"F10.wireOp",EDGE,"E296")}),1.0]])]});
            var Q1;
            Q1=sQuery(id+"F10.wireOp",EDGE,"E296");
            var Q2;
            Q2=sQuery(id+"F9.wireOp",EDGE,"E282");
            sweep(context, id + "F11", {"profiles" : qUnion([Q0]), "surfaceProfiles" : qUnion([Q1]), "path" : qUnion([Q2])});
        }
        {
            var Q0;
            Q0=sQuery(id+"F9.wireOp",EDGE,"E173");
            var Q1;
            Q1=sQuery(id+"F9.wireOp",VERTEX,"E173.start");
            cPlane(context, id + "F12", {"entities" : qUnion([Q0, Q1]), "cplaneType" : CPlaneType.LINE_POINT, "offset" : 25 * mm, "width" : 150 * mm, "height" : 150 * mm});
        }
        {
            var Q0;
            Q0=qCreatedBy(id+"F12.planeOp",FACE);
            var sketch = newSketch(context, id + "F13", { "sketchPlane" : qUnion([Q0])});
            skCircle(sketch, "E297", {"center": v(-9.43, 0.61) * mm, "radius": 0.2 * mm});
            skSolve(sketch);
        }
        {
            var Q0;
            Q0=makeQuery(id+"F13.imprint","IMPRINT",FACE,{"disambiguationData":[TD([[makeQuery(id+"F13.imprint","IMPRINT",EDGE,{"derivedFrom":sQuery(id+"F13.wireOp",EDGE,"E297")}),1.0]])]});
            var Q1;
            Q1=sQuery(id+"F13.wireOp",EDGE,"E297");
            var Q2;
            Q2=sQuery(id+"F9.wireOp",EDGE,"E173");
            var Q3;
            Q3=sQuery(id+"F9.wireOp",EDGE,"E260");
            var Q4;
            Q4=sQuery(id+"F9.wireOp",EDGE,"E177");
            var Q5;
            Q5=sQuery(id+"F9.wireOp",EDGE,"E269");
            var Q6;
            Q6=sQuery(id+"F9.wireOp",EDGE,"E181");
            var Q7;
            Q7=sQuery(id+"F9.wireOp",EDGE,"E261");
            var Q8;
            Q8=sQuery(id+"F9.wireOp",EDGE,"E185");
            var Q9;
            Q9=sQuery(id+"F9.wireOp",EDGE,"E268");
            var Q10;
            Q10=sQuery(id+"F9.wireOp",EDGE,"E189");
            var Q11;
            Q11=sQuery(id+"F9.wireOp",EDGE,"E262");
            var Q12;
            Q12=sQuery(id+"F9.wireOp",EDGE,"E193");
            var Q13;
            Q13=sQuery(id+"F9.wireOp",EDGE,"E267");
            var Q14;
            Q14=sQuery(id+"F9.wireOp",EDGE,"E197");
            var Q15;
            Q15=sQuery(id+"F9.wireOp",EDGE,"E201");
            var Q16;
            Q16=sQuery(id+"F9.wireOp",EDGE,"E266");
            var Q17;
            Q17=sQuery(id+"F9.wireOp",EDGE,"E205");
            var Q18;
            Q18=sQuery(id+"F9.wireOp",EDGE,"E209");
            var Q19;
            Q19=sQuery(id+"F9.wireOp",EDGE,"E265");
            var Q20;
            Q20=sQuery(id+"F9.wireOp",EDGE,"E213");
            var Q21;
            Q21=sQuery(id+"F9.wireOp",EDGE,"E274");
            var Q22;
            Q22=sQuery(id+"F9.wireOp",EDGE,"E290");
            var Q23;
            Q23=sQuery(id+"F9.wireOp",EDGE,"E280");
            var Q24;
            Q24=sQuery(id+"F9.wireOp",EDGE,"E264");
            var Q25;
            Q25=sQuery(id+"F9.wireOp",EDGE,"E263");
            var Q26;
            Q26=sQuery(id+"F9.wireOp",EDGE,"E283");
            var Q27;
            Q27=sQuery(id+"F9.wireOp",EDGE,"E284");
            var Q28;
            Q28=sQuery(id+"F9.wireOp",EDGE,"E217");
            var Q29;
            Q29=sQuery(id+"F9.wireOp",EDGE,"E291");
            var Q30;
            Q30=sQuery(id+"F9.wireOp",EDGE,"E220");
            var Q31;
            Q31=sQuery(id+"F9.wireOp",EDGE,"E224");
            var Q32;
            Q32=sQuery(id+"F9.wireOp",EDGE,"E292");
            var Q33;
            Q33=sQuery(id+"F9.wireOp",EDGE,"E228");
            var Q34;
            Q34=sQuery(id+"F9.wireOp",EDGE,"E232");
            var Q35;
            Q35=sQuery(id+"F9.wireOp",EDGE,"E293");
            var Q36;
            Q36=sQuery(id+"F9.wireOp",EDGE,"E236");
            var Q37;
            Q37=sQuery(id+"F9.wireOp",EDGE,"E240");
            var Q38;
            Q38=sQuery(id+"F9.wireOp",EDGE,"E294");
            var Q39;
            Q39=sQuery(id+"F9.wireOp",EDGE,"E244");
            var Q40;
            Q40=sQuery(id+"F9.wireOp",EDGE,"E248");
            var Q41;
            Q41=sQuery(id+"F9.wireOp",EDGE,"E295");
            var Q42;
            Q42=sQuery(id+"F9.wireOp",EDGE,"E288");
            var Q43;
            Q43=sQuery(id+"F9.wireOp",EDGE,"E287");
            var Q44;
            Q44=sQuery(id+"F9.wireOp",EDGE,"E286");
            var Q45;
            Q45=sQuery(id+"F9.wireOp",EDGE,"E285");
            var Q46;
            Q46=sQuery(id+"F9.wireOp",EDGE,"E252");
            var Q47;
            Q47=sQuery(id+"F9.wireOp",EDGE,"E289");
            var Q48;
            Q48=sQuery(id+"F9.wireOp",EDGE,"E256");
            sweep(context, id + "F14", {"profiles" : qUnion([Q0]), "surfaceProfiles" : qUnion([Q1]), "path" : qUnion([Q2, Q3, Q4, Q5, Q6, Q7, Q8, Q9, Q10, Q11, Q12, Q13, Q14, Q15, Q16, Q17, Q18, Q19, Q20, Q21, Q22, Q23, Q24, Q25, Q26, Q27, Q28, Q29, Q30, Q31, Q32, Q33, Q34, Q35, Q36, Q37, Q38, Q39, Q40, Q41, Q42, Q43, Q44, Q45, Q46, Q47, Q48])});
        }
    });
